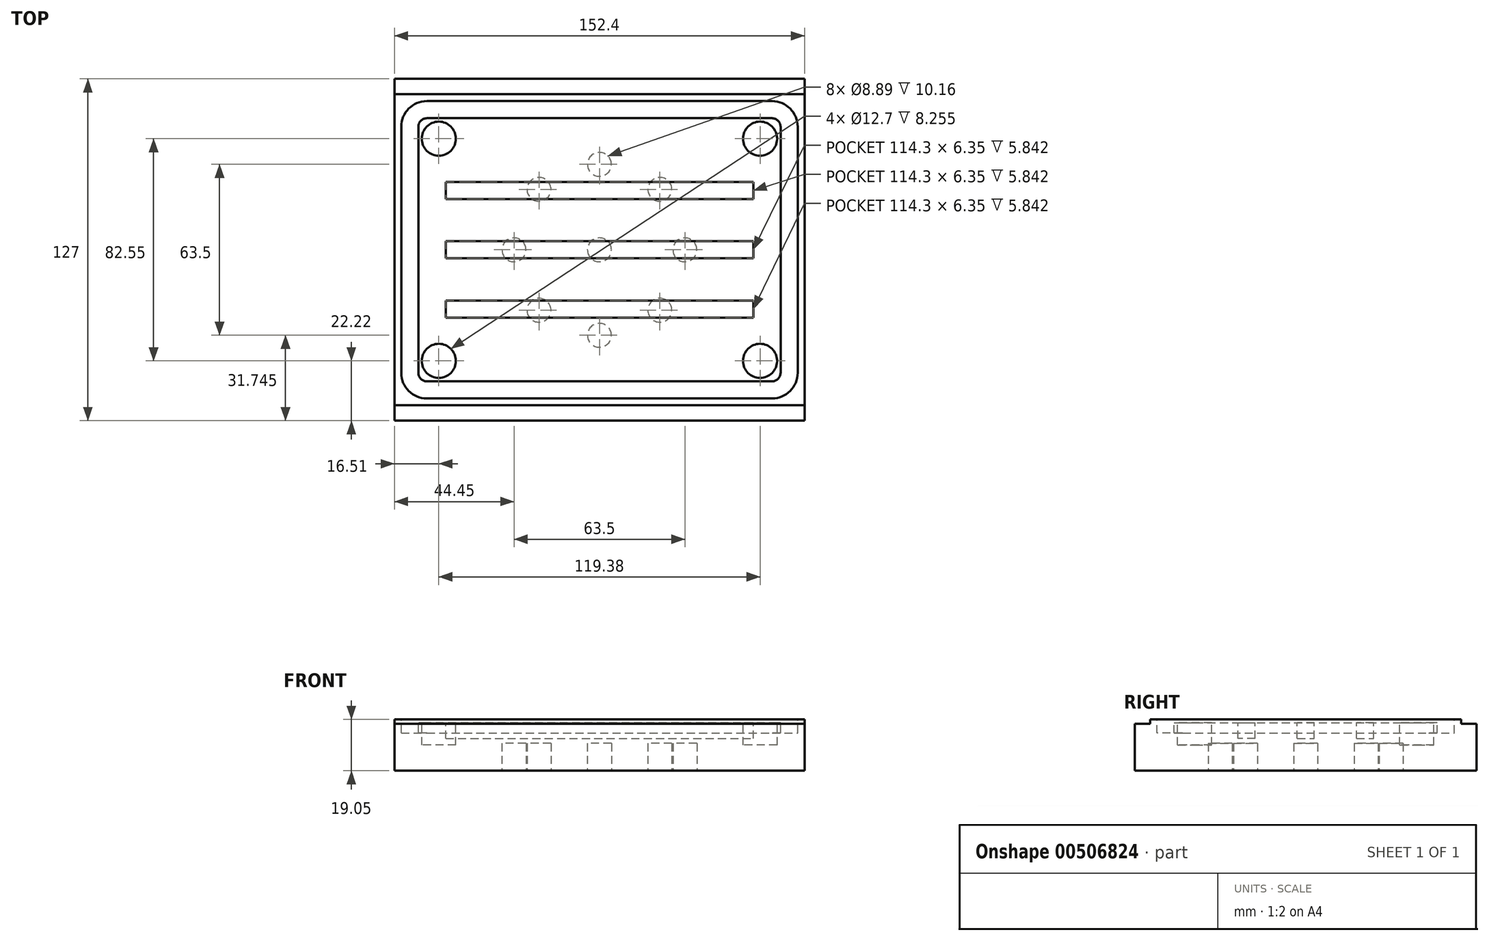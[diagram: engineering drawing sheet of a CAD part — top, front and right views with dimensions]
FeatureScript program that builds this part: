
annotation { "Feature Type Name" : "Feature", "Feature Type Description" : "" }
export const myFeature = defineFeature(function(context is Context, id is Id, definition is map)
    precondition{}
    {
        {
            var Q0;
            Q0=qCreatedBy(makeId("Top.planeOp"),FACE);
            var sketch = newSketch(context, id + "F0", { "sketchPlane" : qUnion([Q0])});
            skLineSegment(sketch, "E0.bottom", {"start": v(0, 0) * mm, "end": v(152.4, 0) * mm});
            skLineSegment(sketch, "E0.top", {"start": v(0, 115.57) * mm, "end": v(152.4, 115.57) * mm});
            skLineSegment(sketch, "E0.left", {"start": v(0, 0) * mm, "end": v(0, 115.57) * mm});
            skLineSegment(sketch, "E0.right", {"start": v(152.4, 0) * mm, "end": v(152.4, 115.57) * mm});
            skPoint(sketch, "E1.visualSharp", {"position": v(0, 115.57) * mm});
            skPoint(sketch, "E2.visualSharp", {"position": v(152.4, 115.57) * mm});
            skPoint(sketch, "E3.visualSharp", {"position": v(152.4, 0) * mm});
            skPoint(sketch, "E4.visualSharp", {"position": v(0, 0) * mm});
            skSolve(sketch);
        }
        {
            var Q0;
            Q0 = qSketchRegion(id + "F0", true);
            extrude(context, id + "F1", {"entities" : qUnion([Q0]), "depth" : 19.05 * mm, "offsetDistance" : 25.4 * mm});
        }
        {
            var Q0;
            Q0=makeQuery(id+"F1.opExtrude","CAP_FACE",FACE,{"disambiguationData":[OSD([sQuery(id+"F0.wireOp",EDGE,"E0.bottom"),sQuery(id+"F0.wireOp",EDGE,"E0.top"),sQuery(id+"F0.wireOp",EDGE,"E0.left"),sQuery(id+"F0.wireOp",EDGE,"E0.right")])],"isStart":false});
            var sketch = newSketch(context, id + "F2", { "sketchPlane" : qUnion([Q0])});
            skLineSegment(sketch, "E5.0", {"start": v(12.06, 113.03) * mm, "end": v(140.33, 113.03) * mm});
            skLineSegment(sketch, "E5.1", {"start": v(2.54, 12.06) * mm, "end": v(2.54, 103.5) * mm});
            skLineSegment(sketch, "E5.2", {"start": v(12.06, 2.54) * mm, "end": v(140.33, 2.54) * mm});
            skLineSegment(sketch, "E5.3", {"start": v(149.86, 12.06) * mm, "end": v(149.86, 103.5) * mm});
            skPoint(sketch, "E6.visualSharp", {"position": v(2.54, 113.03) * mm});
            skArc(sketch, "E6.filletArc", {"start": v(12.07, 113.03) * mm, "mid": v(5.33, 110.24) * mm, "end": v(2.54, 103.5) * mm});
            skPoint(sketch, "E7.visualSharp", {"position": v(2.54, 2.54) * mm});
            skArc(sketch, "E7.filletArc", {"start": v(2.54, 12.06) * mm, "mid": v(5.33, 5.33) * mm, "end": v(12.06, 2.54) * mm});
            skPoint(sketch, "E8.visualSharp", {"position": v(149.86, 2.54) * mm});
            skArc(sketch, "E8.filletArc", {"start": v(140.33, 2.54) * mm, "mid": v(147.07, 5.33) * mm, "end": v(149.86, 12.07) * mm});
            skPoint(sketch, "E9.visualSharp", {"position": v(149.86, 113.03) * mm});
            skArc(sketch, "E9.filletArc", {"start": v(149.86, 103.5) * mm, "mid": v(147.07, 110.24) * mm, "end": v(140.33, 113.03) * mm});
            skArc(sketch, "E10.0", {"start": v(12.07, 106.68) * mm, "mid": v(9.82, 105.75) * mm, "end": v(8.89, 103.5) * mm});
            skLineSegment(sketch, "E10.1", {"start": v(8.89, 12.06) * mm, "end": v(8.89, 103.5) * mm});
            skLineSegment(sketch, "E10.2", {"start": v(12.06, 106.68) * mm, "end": v(140.33, 106.68) * mm});
            skArc(sketch, "E10.3", {"start": v(8.89, 12.06) * mm, "mid": v(9.82, 9.82) * mm, "end": v(12.07, 8.89) * mm});
            skArc(sketch, "E10.4", {"start": v(143.5, 103.5) * mm, "mid": v(142.58, 105.75) * mm, "end": v(140.33, 106.68) * mm});
            skLineSegment(sketch, "E10.5", {"start": v(143.5, 12.06) * mm, "end": v(143.5, 103.5) * mm});
            skArc(sketch, "E10.6", {"start": v(140.33, 8.89) * mm, "mid": v(142.58, 9.82) * mm, "end": v(143.5, 12.07) * mm});
            skLineSegment(sketch, "E10.7", {"start": v(12.06, 8.89) * mm, "end": v(140.33, 8.89) * mm});
            skSolve(sketch);
        }
        {
            var Q0;
            Q0 = qSketchRegion(id + "F2", true);
            extrude(context, id + "F3", {"entities" : qUnion([Q0]), "operationType" : NewBodyOperationType.REMOVE, "oppositeDirection" : true, "depth" : 5.08 * mm, "offsetDistance" : 25.4 * mm});
        }
        {
            var Q0;
            Q0=makeQuery(id+"F3.boolean.opBoolean","SPLIT",FACE,{"disambiguationData":[TD([makeQuery(id+"F3.opExtrude","SWEPT_FACE",FACE,{"disambiguationData":[OSD([sQuery(id+"F2.wireOp",EDGE,"E10.0")])]})])],"derivedFrom":makeQuery(id+"F1.opExtrude","CAP_FACE",FACE,{"disambiguationData":[OSD([sQuery(id+"F0.wireOp",EDGE,"E0.bottom"),sQuery(id+"F0.wireOp",EDGE,"E0.top"),sQuery(id+"F0.wireOp",EDGE,"E0.left"),sQuery(id+"F0.wireOp",EDGE,"E0.right"),sQuery(id+"F0.wireOp",EDGE,"E1.filletArc"),sQuery(id+"F0.wireOp",EDGE,"E2.filletArc"),sQuery(id+"F0.wireOp",EDGE,"E3.filletArc"),sQuery(id+"F0.wireOp",EDGE,"E4.filletArc")])],"isStart":false})});
            var sketch = newSketch(context, id + "F4", { "sketchPlane" : qUnion([Q0])});
            skLineSegment(sketch, "E11", {"start": v(8.89, 57.78) * mm, "end": v(143.5, 57.78) * mm, "construction": true});
            skLineSegment(sketch, "E12", {"start": v(8.89, 35.78) * mm, "end": v(143.5, 35.78) * mm, "construction": true});
            skLineSegment(sketch, "E13.bottom", {"start": v(19.05, 38.96) * mm, "end": v(133.35, 38.96) * mm});
            skLineSegment(sketch, "E13.top", {"start": v(19.05, 32.61) * mm, "end": v(133.35, 32.61) * mm});
            skLineSegment(sketch, "E13.left", {"start": v(19.05, 38.96) * mm, "end": v(19.05, 32.61) * mm});
            skLineSegment(sketch, "E13.right", {"start": v(133.35, 38.96) * mm, "end": v(133.35, 32.61) * mm});
            skPoint(sketch, "E13.middle", {"position": v(76.2, 35.78) * mm});
            skLineSegment(sketch, "E14.bottom", {"start": v(19.05, 54.61) * mm, "end": v(133.35, 54.61) * mm});
            skLineSegment(sketch, "E14.top", {"start": v(19.05, 60.96) * mm, "end": v(133.35, 60.96) * mm});
            skLineSegment(sketch, "E14.left", {"start": v(19.05, 54.61) * mm, "end": v(19.05, 60.96) * mm});
            skLineSegment(sketch, "E14.right", {"start": v(133.35, 54.61) * mm, "end": v(133.35, 60.96) * mm});
            skPoint(sketch, "E14.middle", {"position": v(76.2, 57.78) * mm});
            skLineSegment(sketch, "E15.MirrorCS", {"start": v(8.89, 79.78) * mm, "end": v(143.5, 79.78) * mm, "construction": true});
            skLineSegment(sketch, "E16.MirrorCS", {"start": v(19.05, 76.6) * mm, "end": v(133.35, 76.6) * mm});
            skLineSegment(sketch, "E17.MirrorCS", {"start": v(19.05, 82.96) * mm, "end": v(133.35, 82.96) * mm});
            skLineSegment(sketch, "E18.MirrorCS", {"start": v(133.35, 76.6) * mm, "end": v(133.35, 82.96) * mm});
            skLineSegment(sketch, "E19.MirrorCS", {"start": v(19.05, 76.6) * mm, "end": v(19.05, 82.96) * mm});
            skSolve(sketch);
        }
        {
            var Q0;
            Q0=makeQuery(id+"F4.imprint","IMPRINT",FACE,{"disambiguationData":[TD([[makeQuery(id+"F4.imprint","IMPRINT",EDGE,{"derivedFrom":sQuery(id+"F4.wireOp",EDGE,"E14.bottom")}),1.0]])]});
            var Q1;
            Q1=makeQuery(id+"F4.imprint","IMPRINT",FACE,{"disambiguationData":[TD([[makeQuery(id+"F4.imprint","IMPRINT",EDGE,{"derivedFrom":sQuery(id+"F4.wireOp",EDGE,"E16.MirrorCS")}),1.0]])]});
            var Q2;
            Q2=makeQuery(id+"F4.imprint","IMPRINT",FACE,{"disambiguationData":[TD([[makeQuery(id+"F4.imprint","IMPRINT",EDGE,{"derivedFrom":sQuery(id+"F4.wireOp",EDGE,"E13.bottom")}),-1.0]])]});
            var Q3;
            Q3=sQuery(id+"F4.wireOp",EDGE,"E16.MirrorCS");
            var Q4;
            Q4=sQuery(id+"F4.wireOp",EDGE,"E19.MirrorCS");
            var Q5;
            Q5=sQuery(id+"F4.wireOp",EDGE,"E17.MirrorCS");
            var Q6;
            Q6=sQuery(id+"F4.wireOp",EDGE,"E18.MirrorCS");
            var Q7;
            Q7=sQuery(id+"F4.wireOp",EDGE,"E14.right");
            var Q8;
            Q8=sQuery(id+"F4.wireOp",EDGE,"E14.top");
            var Q9;
            Q9=sQuery(id+"F4.wireOp",EDGE,"E14.bottom");
            var Q10;
            Q10=sQuery(id+"F4.wireOp",EDGE,"E13.bottom");
            var Q11;
            Q11=sQuery(id+"F4.wireOp",EDGE,"E13.right");
            var Q12;
            Q12=sQuery(id+"F4.wireOp",EDGE,"E13.top");
            var Q13;
            Q13=sQuery(id+"F4.wireOp",EDGE,"E13.left");
            var Q14;
            Q14=sQuery(id+"F4.wireOp",EDGE,"E14.left");
            extrude(context, id + "F5", {"entities" : qUnion([Q0, Q1, Q2]), "operationType" : NewBodyOperationType.REMOVE, "surfaceEntities" : qUnion([Q3, Q4, Q5, Q6, Q7, Q8, Q9, Q10, Q11, Q12, Q13, Q14]), "oppositeDirection" : true, "depth" : 7.11 * mm, "offsetDistance" : 25.4 * mm});
        }
        {
            var Q0;
            Q0=makeQuery(id+"F2.imprint","IMPRINT",FACE,{"disambiguationData":[TD([[makeQuery(id+"F2.imprint","IMPRINT",EDGE,{"derivedFrom":sQuery(id+"F2.wireOp",EDGE,"E10.0")}),1.0]])]});
            var Q1;
            Q1=sQuery(id+"F2.wireOp",EDGE,"E10.1");
            var Q2;
            Q2=sQuery(id+"F2.wireOp",EDGE,"E10.0");
            var Q3;
            Q3=sQuery(id+"F2.wireOp",EDGE,"E10.2");
            var Q4;
            Q4=sQuery(id+"F2.wireOp",EDGE,"E10.4");
            var Q5;
            Q5=sQuery(id+"F2.wireOp",EDGE,"E10.5");
            var Q6;
            Q6=sQuery(id+"F2.wireOp",EDGE,"E10.6");
            var Q7;
            Q7=sQuery(id+"F2.wireOp",EDGE,"E10.7");
            var Q8;
            Q8=sQuery(id+"F2.wireOp",EDGE,"E10.3");
            extrude(context, id + "F6", {"entities" : qUnion([Q0]), "operationType" : NewBodyOperationType.REMOVE, "surfaceEntities" : qUnion([Q1, Q2, Q3, Q4, Q5, Q6, Q7, Q8]), "oppositeDirection" : true, "depth" : 0.8 * mm, "offsetDistance" : 25.4 * mm});
        }
        {
            var Q0;
            Q0=makeQuery(id+"F0.imprint","IMPRINT",FACE,{"disambiguationData":[TD([[makeQuery(id+"F0.imprint","IMPRINT",EDGE,{"derivedFrom":sQuery(id+"F0.wireOp",EDGE,"E0.bottom")}),1.0]])]});
            var sketch = newSketch(context, id + "F7", { "sketchPlane" : qUnion([Q0])});
            skLineSegment(sketch, "E20.bottom", {"start": v(0, 0) * mm, "end": v(152.4, 0) * mm});
            skLineSegment(sketch, "E20.top", {"start": v(0, -5.72) * mm, "end": v(152.4, -5.72) * mm});
            skLineSegment(sketch, "E20.left", {"start": v(0, 0) * mm, "end": v(0, -5.72) * mm});
            skLineSegment(sketch, "E20.right", {"start": v(152.4, 0) * mm, "end": v(152.4, -5.72) * mm});
            skLineSegment(sketch, "E21.MirrorCS", {"start": v(0, 115.57) * mm, "end": v(152.4, 115.57) * mm});
            skLineSegment(sketch, "E22.MirrorCS", {"start": v(0, 121.28) * mm, "end": v(152.4, 121.28) * mm});
            skLineSegment(sketch, "E23.MirrorCS", {"start": v(152.4, 115.57) * mm, "end": v(152.4, 121.28) * mm});
            skLineSegment(sketch, "E24.MirrorCS", {"start": v(0, 115.57) * mm, "end": v(0, 121.28) * mm});
            skSolve(sketch);
        }
        {
            var Q0;
            Q0=makeQuery(id+"F7.imprint","IMPRINT",FACE,{"disambiguationData":[TD([[makeQuery(id+"F7.imprint","IMPRINT",EDGE,{"derivedFrom":sQuery(id+"F7.wireOp",EDGE,"E20.bottom")}),-1.0]])]});
            var Q1;
            Q1=makeQuery(id+"F7.imprint","IMPRINT",FACE,{"disambiguationData":[TD([[makeQuery(id+"F7.imprint","IMPRINT",EDGE,{"derivedFrom":sQuery(id+"F7.wireOp",EDGE,"E21.MirrorCS")}),1.0]])]});
            extrude(context, id + "F8", {"entities" : qUnion([Q0, Q1]), "operationType" : NewBodyOperationType.ADD, "depth" : 17.46 * mm, "offsetDistance" : 25.4 * mm});
        }
        {
            var Q0;
            Q0=makeQuery(id+"F2.imprint","IMPRINT",FACE,{"disambiguationData":[TD([[makeQuery(id+"F2.imprint","IMPRINT",EDGE,{"derivedFrom":sQuery(id+"F2.wireOp",EDGE,"E10.0")}),1.0]])]});
            extrude(context, id + "F9", {"entities" : qUnion([Q0]), "operationType" : NewBodyOperationType.REMOVE, "oppositeDirection" : true, "depth" : 1.27 * mm, "offsetDistance" : 25.4 * mm});
        }
        {
            var Q0;
            Q0=makeQuery(id+"F2.imprint","IMPRINT",FACE,{"disambiguationData":[TD([[makeQuery(id+"F2.imprint","IMPRINT",EDGE,{"derivedFrom":sQuery(id+"F2.wireOp",EDGE,"E10.0")}),1.0]])]});
            var sketch = newSketch(context, id + "F10", { "sketchPlane" : qUnion([Q0])});
            skCircle(sketch, "E25", {"center": v(16.5, 99.06) * mm, "radius": 6.35 * mm});
            skCircle(sketch, "E26", {"center": v(135.9, 99.06) * mm, "radius": 6.35 * mm});
            skLineSegment(sketch, "E27.bottom", {"start": v(16.5, 99.06) * mm, "end": v(135.9, 99.06) * mm, "construction": true});
            skLineSegment(sketch, "E27.top", {"start": v(16.51, 16.5) * mm, "end": v(135.9, 16.5) * mm, "construction": true});
            skLineSegment(sketch, "E27.left", {"start": v(16.5, 99.06) * mm, "end": v(16.51, 16.5) * mm, "construction": true});
            skLineSegment(sketch, "E27.right", {"start": v(135.9, 99.06) * mm, "end": v(135.9, 16.5) * mm, "construction": true});
            skCircle(sketch, "E28.MirrorC", {"center": v(16.51, 16.5) * mm, "radius": 6.35 * mm});
            skCircle(sketch, "E29.MirrorC", {"center": v(135.9, 16.5) * mm, "radius": 6.35 * mm});
            skSolve(sketch);
        }
        {
            var Q0;
            Q0 = qSketchRegion(id + "F10", true);
            extrude(context, id + "F11", {"entities" : qUnion([Q0]), "operationType" : NewBodyOperationType.REMOVE, "oppositeDirection" : true, "depth" : 9.52 * mm, "offsetDistance" : 25.4 * mm});
        }
        {
            var Q0;
            Q0=makeQuery(id+"F0.imprint","IMPRINT",FACE,{"disambiguationData":[TD([[makeQuery(id+"F0.imprint","IMPRINT",EDGE,{"derivedFrom":sQuery(id+"F0.wireOp",EDGE,"E0.bottom")}),1.0]])]});
            var sketch = newSketch(context, id + "F12", { "sketchPlane" : qUnion([Q0])});
            skCircle(sketch, "E30", {"center": v(76.2, 57.78) * mm, "radius": 4.45 * mm});
            skCircle(sketch, "E31", {"center": v(44.45, 57.78) * mm, "radius": 4.45 * mm});
            skCircle(sketch, "E32.1.0", {"center": v(53.75, 35.33) * mm, "radius": 4.45 * mm});
            skCircle(sketch, "E32.2.0", {"center": v(76.2, 26.03) * mm, "radius": 4.45 * mm});
            skCircle(sketch, "E32.3.0", {"center": v(98.65, 35.33) * mm, "radius": 4.45 * mm});
            skCircle(sketch, "E32.4.0", {"center": v(107.95, 57.78) * mm, "radius": 4.45 * mm});
            skCircle(sketch, "E32.5.0", {"center": v(98.65, 80.24) * mm, "radius": 4.45 * mm});
            skCircle(sketch, "E32.6.0", {"center": v(76.2, 89.53) * mm, "radius": 4.45 * mm});
            skCircle(sketch, "E32.7.0", {"center": v(53.75, 80.24) * mm, "radius": 4.45 * mm});
            skSolve(sketch);
        }
        {
            var Q0;
            Q0 = qSketchRegion(id + "F12", true);
            extrude(context, id + "F13", {"entities" : qUnion([Q0]), "operationType" : NewBodyOperationType.REMOVE, "depth" : 10.16 * mm, "offsetDistance" : 25.4 * mm});
        }
    });
